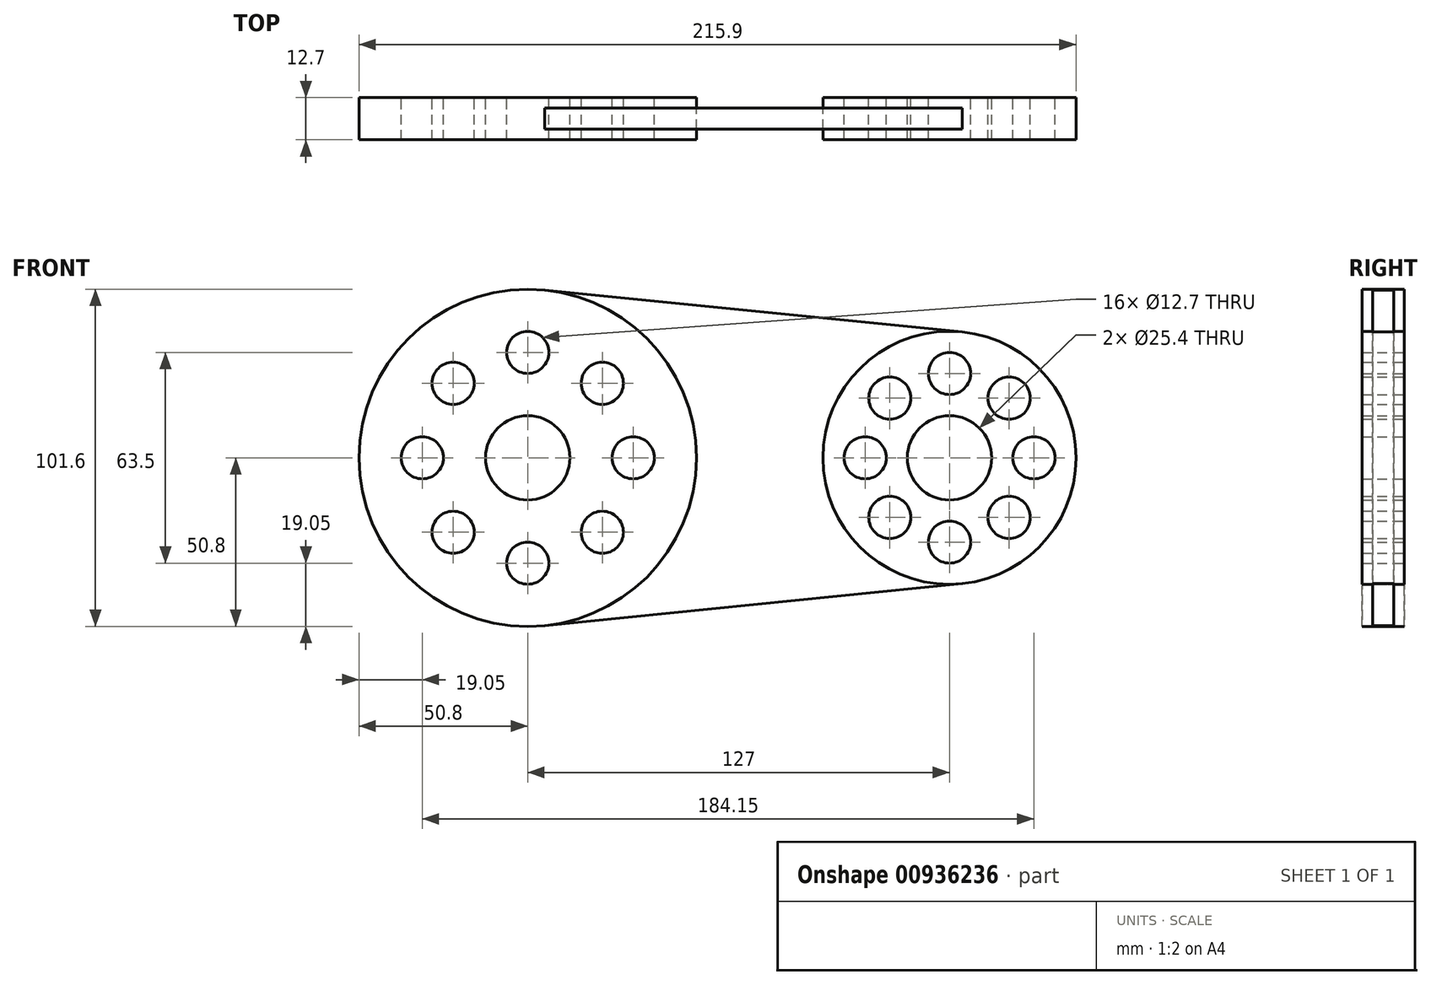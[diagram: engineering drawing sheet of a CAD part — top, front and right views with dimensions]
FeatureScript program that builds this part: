
annotation { "Feature Type Name" : "Feature", "Feature Type Description" : "" }
export const myFeature = defineFeature(function(context is Context, id is Id, definition is map)
    precondition{}
    {
        {
            var Q0;
            Q0=qCreatedBy(makeId("Front.planeOp"),FACE);
            var sketch = newSketch(context, id + "F0", { "sketchPlane" : qUnion([Q0])});
            skCircle(sketch, "E0", {"center": v(0, 0) * mm, "radius": 50.8 * mm});
            skCircle(sketch, "E1", {"center": v(0, 0) * mm, "radius": 12.7 * mm});
            skLineSegment(sketch, "E2", {"start": v(0, 0) * mm, "end": v(171.68, 0) * mm, "construction": true});
            skCircle(sketch, "E3", {"center": v(127, 0) * mm, "radius": 12.7 * mm});
            skCircle(sketch, "E4", {"center": v(127, 0) * mm, "radius": 38.1 * mm});
            skLineSegment(sketch, "E5", {"start": v(5.08, 50.55) * mm, "end": v(130.8, 37.9) * mm});
            skLineSegment(sketch, "E6.MirrorCS", {"start": v(5.08, -50.55) * mm, "end": v(130.8, -37.9) * mm});
            skCircle(sketch, "E7", {"center": v(0, 0) * mm, "radius": 31.75 * mm, "construction": true});
            skCircle(sketch, "E8", {"center": v(0, 31.75) * mm, "radius": 6.35 * mm});
            skCircle(sketch, "E9.1.0", {"center": v(-22.45, 22.45) * mm, "radius": 6.35 * mm});
            skCircle(sketch, "E9.2.0", {"center": v(-31.75, 0) * mm, "radius": 6.35 * mm});
            skCircle(sketch, "E9.3.0", {"center": v(-22.45, -22.45) * mm, "radius": 6.35 * mm});
            skCircle(sketch, "E9.4.0", {"center": v(0, -31.75) * mm, "radius": 6.35 * mm});
            skCircle(sketch, "E9.5.0", {"center": v(22.45, -22.45) * mm, "radius": 6.35 * mm});
            skCircle(sketch, "E9.6.0", {"center": v(31.75, 0) * mm, "radius": 6.35 * mm});
            skCircle(sketch, "E9.7.0", {"center": v(22.45, 22.45) * mm, "radius": 6.35 * mm});
            skCircle(sketch, "E10", {"center": v(101.6, 0) * mm, "radius": 6.35 * mm});
            skCircle(sketch, "E11.1.0", {"center": v(109.04, -17.96) * mm, "radius": 6.35 * mm});
            skCircle(sketch, "E11.2.0", {"center": v(127, -25.4) * mm, "radius": 6.35 * mm});
            skCircle(sketch, "E11.3.0", {"center": v(144.96, -17.96) * mm, "radius": 6.35 * mm});
            skCircle(sketch, "E11.4.0", {"center": v(152.4, 0) * mm, "radius": 6.35 * mm});
            skCircle(sketch, "E11.5.0", {"center": v(144.96, 17.96) * mm, "radius": 6.35 * mm});
            skCircle(sketch, "E11.6.0", {"center": v(127, 25.4) * mm, "radius": 6.35 * mm});
            skCircle(sketch, "E11.7.0", {"center": v(109.04, 17.96) * mm, "radius": 6.35 * mm});
            skSolve(sketch);
        }
        {
            var Q0;
            Q0=makeQuery(id+"F0.imprint","IMPRINT",FACE,{"disambiguationData":[TD([[makeQuery(id+"F0.imprint","IMPRINT",EDGE,{"derivedFrom":sQuery(id+"F0.wireOp",EDGE,"E1")}),-1.0]])]});
            var Q1;
            Q1=makeQuery(id+"F0.imprint","IMPRINT",FACE,{"disambiguationData":[TD([[makeQuery(id+"F0.imprint","IMPRINT",EDGE,{"derivedFrom":sQuery(id+"F0.wireOp",EDGE,"E3")}),-1.0]])]});
            extrude(context, id + "F1", {"entities" : qUnion([Q0, Q1]), "endBound" : BoundingType.SYMMETRIC, "depth" : 12.7 * mm, "offsetDistance" : 25.4 * mm});
        }
        {
            var Q0;
            {var subQ0=sQuery(id+"F0.wireOp",EDGE,"E5");Q0=makeQuery(id+"F0.imprint","IMPRINT",FACE,{"disambiguationData":[TD([[makeQuery(id+"F0.imprint","IMPRINT",EDGE,{"derivedFrom":subQ0}),-1.0]])]});}
            extrude(context, id + "F2", {"entities" : qUnion([Q0]), "endBound" : BoundingType.SYMMETRIC, "depth" : 6.35 * mm, "offsetDistance" : 25.4 * mm});
        }
    });
